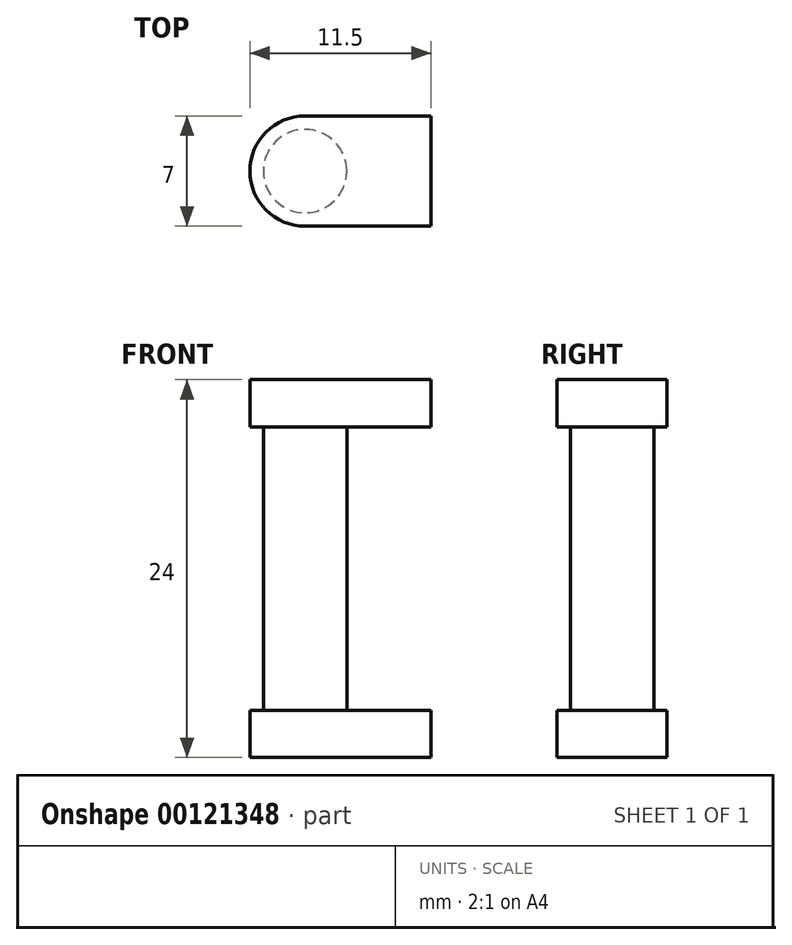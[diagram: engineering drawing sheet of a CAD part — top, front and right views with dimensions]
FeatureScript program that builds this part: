
annotation { "Feature Type Name" : "Feature", "Feature Type Description" : "" }
export const myFeature = defineFeature(function(context is Context, id is Id, definition is map)
    precondition{}
    {
        {
            var Q0;
            Q0=qCreatedBy(makeId("Top.planeOp"),FACE);
            var sketch = newSketch(context, id + "F0", { "sketchPlane" : qUnion([Q0])});
            skCircle(sketch, "E0", {"center": v(0, 0) * mm, "radius": 2.65 * mm});
            skSolve(sketch);
        }
        {
            var Q0;
            Q0 = qSketchRegion(id + "F0", true);
            extrude(context, id + "F1", {"entities" : qUnion([Q0]), "oppositeDirection" : true, "depth" : 18 * mm});
        }
        {
            var Q0;
            Q0=makeQuery(id+"F1.opExtrude","CAP_FACE",FACE,{"disambiguationData":[OSD([sQuery(id+"F0.wireOp",EDGE,"E0")])],"isStart":true});
            var sketch = newSketch(context, id + "F2", { "sketchPlane" : qUnion([Q0])});
            skCircle(sketch, "E1", {"center": v(0, 0) * mm, "radius": 3.5 * mm});
            skSolve(sketch);
        }
        {
            var Q0;
            Q0 = qSketchRegion(id + "F2", true);
            extrude(context, id + "F3", {"entities" : qUnion([Q0]), "operationType" : NewBodyOperationType.ADD, "depth" : 3 * mm});
        }
        {
            var Q0;
            Q0=makeQuery(id+"F1.opExtrude","CAP_FACE",FACE,{"disambiguationData":[OSD([sQuery(id+"F0.wireOp",EDGE,"E0")])],"isStart":false});
            var sketch = newSketch(context, id + "F4", { "sketchPlane" : qUnion([Q0])});
            skCircle(sketch, "E2", {"center": v(0, 0) * mm, "radius": 3.5 * mm});
            skSolve(sketch);
        }
        {
            var Q0;
            Q0 = qSketchRegion(id + "F4", true);
            extrude(context, id + "F5", {"entities" : qUnion([Q0]), "operationType" : NewBodyOperationType.ADD, "depth" : 3 * mm});
        }
        {
            var Q0;
            Q0=makeQuery(id+"F3.opExtrude","CAP_FACE",FACE,{"disambiguationData":[OSD([sQuery(id+"F2.wireOp",EDGE,"E1")])],"isStart":false});
            var sketch = newSketch(context, id + "F6", { "sketchPlane" : qUnion([Q0])});
            skLineSegment(sketch, "E3.bottom", {"start": v(0, 3.5) * mm, "end": v(8, 3.5) * mm});
            skLineSegment(sketch, "E3.top", {"start": v(0, -3.5) * mm, "end": v(8, -3.5) * mm});
            skLineSegment(sketch, "E3.left", {"start": v(0, 3.5) * mm, "end": v(0, -3.5) * mm});
            skLineSegment(sketch, "E3.right", {"start": v(8, 3.5) * mm, "end": v(8, -3.5) * mm});
            skSolve(sketch);
        }
        {
            var Q0;
            Q0 = qSketchRegion(id + "F6", true);
            extrude(context, id + "F7", {"entities" : qUnion([Q0]), "operationType" : NewBodyOperationType.ADD, "oppositeDirection" : true, "depth" : 3 * mm});
        }
        {
            var Q0;
            Q0=makeQuery(id+"F5.opExtrude","CAP_FACE",FACE,{"disambiguationData":[OSD([sQuery(id+"F4.wireOp",EDGE,"E2")])],"isStart":false});
            var sketch = newSketch(context, id + "F8", { "sketchPlane" : qUnion([Q0])});
            skLineSegment(sketch, "E4.bottom", {"start": v(0, 3.5) * mm, "end": v(8, 3.5) * mm});
            skLineSegment(sketch, "E4.top", {"start": v(0, -3.5) * mm, "end": v(8, -3.5) * mm});
            skLineSegment(sketch, "E4.left", {"start": v(0, 3.5) * mm, "end": v(0, -3.5) * mm});
            skLineSegment(sketch, "E4.right", {"start": v(8, 3.5) * mm, "end": v(8, -3.5) * mm});
            skSolve(sketch);
        }
        {
            var Q0;
            Q0 = qSketchRegion(id + "F8", true);
            extrude(context, id + "F9", {"entities" : qUnion([Q0]), "operationType" : NewBodyOperationType.ADD, "oppositeDirection" : true, "depth" : 3 * mm});
        }
    });
